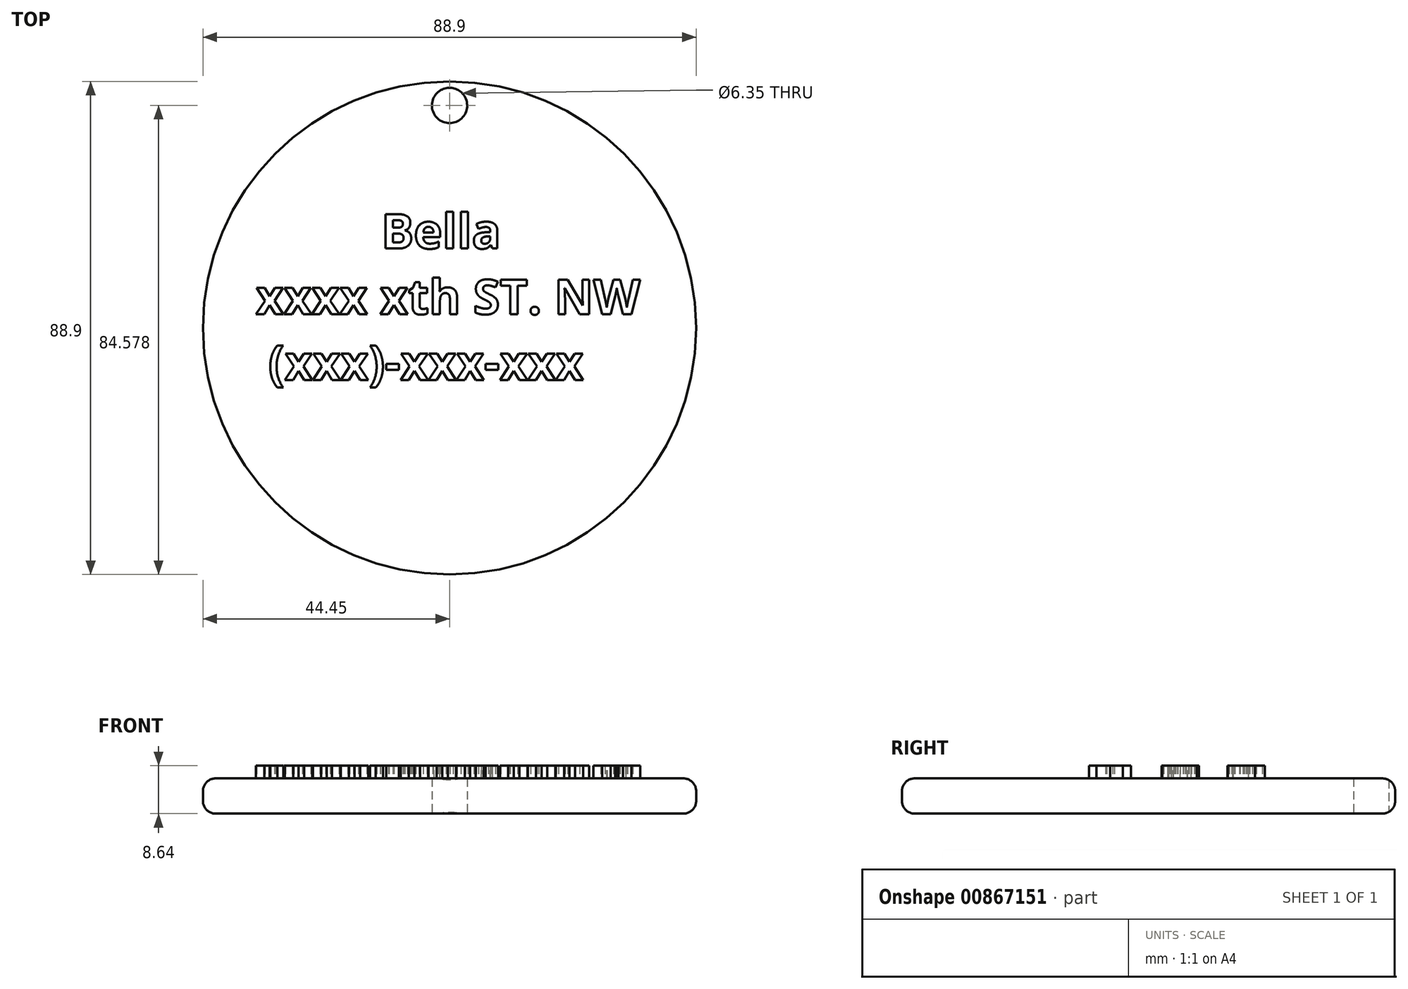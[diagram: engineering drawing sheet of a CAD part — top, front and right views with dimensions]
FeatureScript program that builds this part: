
annotation { "Feature Type Name" : "Feature", "Feature Type Description" : "" }
export const myFeature = defineFeature(function(context is Context, id is Id, definition is map)
    precondition{}
    {
        {
            var Q0;
            Q0=qCreatedBy(makeId("Top.planeOp"),FACE);
            var sketch = newSketch(context, id + "F0", { "sketchPlane" : qUnion([Q0])});
            skCircle(sketch, "E0", {"center": v(0, 0) * mm, "radius": 44.45 * mm});
            skSolve(sketch);
        }
        {
            var Q0;
            Q0=qSketchRegion(id+"F0",true);
            extrude(context, id + "F1", {"entities" : qUnion([Q0]), "endBound" : BoundingType.SYMMETRIC, "depth" : 6.35 * mm, "offsetDistance" : 25.4 * mm});
        }
        {
            var Q0;
            Q0=qCreatedBy(makeId("Top.planeOp"),FACE);
            var sketch = newSketch(context, id + "F2", { "sketchPlane" : qUnion([Q0])});
            skCircle(sketch, "E1", {"center": v(0, 40.13) * mm, "radius": 3.18 * mm});
            skSolve(sketch);
        }
        {
            var Q0;
            Q0=qSketchRegion(id+"F2",true);
            extrude(context, id + "F3", {"entities" : qUnion([Q0]), "operationType" : NewBodyOperationType.REMOVE, "endBound" : BoundingType.SYMMETRIC, "depth" : 25.4 * mm, "offsetDistance" : 25.4 * mm});
        }
        {
            var Q0;
            Q0=makeQuery(id+"F1.opExtrude","CAP_FACE",FACE,{"disambiguationData":[OSD([sQuery(id+"F0.wireOp",EDGE,"E0")])],"isStart":false});
            var sketch = newSketch(context, id + "F4", { "sketchPlane" : qUnion([Q0])});
            skPoint(sketch, "E2", {"position": v(0, 43.3) * mm});
            skPoint(sketch, "E3", {"position": v(-10.03, 43.3) * mm});
            skPoint(sketch, "E4", {"position": v(10.03, 43.3) * mm});
            skSolve(sketch);
        }
        {
            var Q0;
            Q0=makeQuery(id+"F1.opExtrude","CAP_EDGE",EDGE,{"disambiguationData":[OSD([sQuery(id+"F0.wireOp",EDGE,"E0")])],"isStart":false});
            var Q1;
            Q1=makeQuery(id+"F1.opExtrude","CAP_EDGE",EDGE,{"disambiguationData":[OSD([sQuery(id+"F0.wireOp",EDGE,"E0")])],"isStart":true});
            fillet(context, id + "F5", {"entities" : qUnion([Q0, Q1]), "radius" : 2.3 * mm, "tangentPropagation" : true, "allowEdgeOverflow" : false});
        }
        {
            var Q0;
            {var subQ0=sQuery(id+"F0.wireOp",EDGE,"E0");Q0=makeQuery(id+"F4.imprint","IMPRINT",FACE,{"disambiguationData":[TD([[makeQuery(id+"F4.imprint","IMPRINT",EDGE,{"derivedFrom":makeQuery(id+"F1.opExtrude","CAP_EDGE",EDGE,{"disambiguationData":[OSD([subQ0])],"isStart":false})}),1.0]])]});}
            var sketch = newSketch(context, id + "F6", { "sketchPlane" : qUnion([Q0])});
            skText(sketch, "E5", { "text": "          Bella\nxxxx xth ST. NW\n (xxx)-xxx-xxx", "fontName": "OpenSans-Bold.ttf"});
            const initialGuessF6  = {"E5": [-0.03493, 0.01432, 1, 0, 0.00627]};
            skSetInitialGuess(sketch, initialGuessF6);
            skSolve(sketch);
        }
        {
            var Q0;
            Q0 = qSketchRegion(id + "F6", true);
            extrude(context, id + "F7", {"entities" : qUnion([Q0]), "operationType" : NewBodyOperationType.ADD, "depth" : 2.3 * mm, "offsetDistance" : 25.4 * mm});
        }
    });
